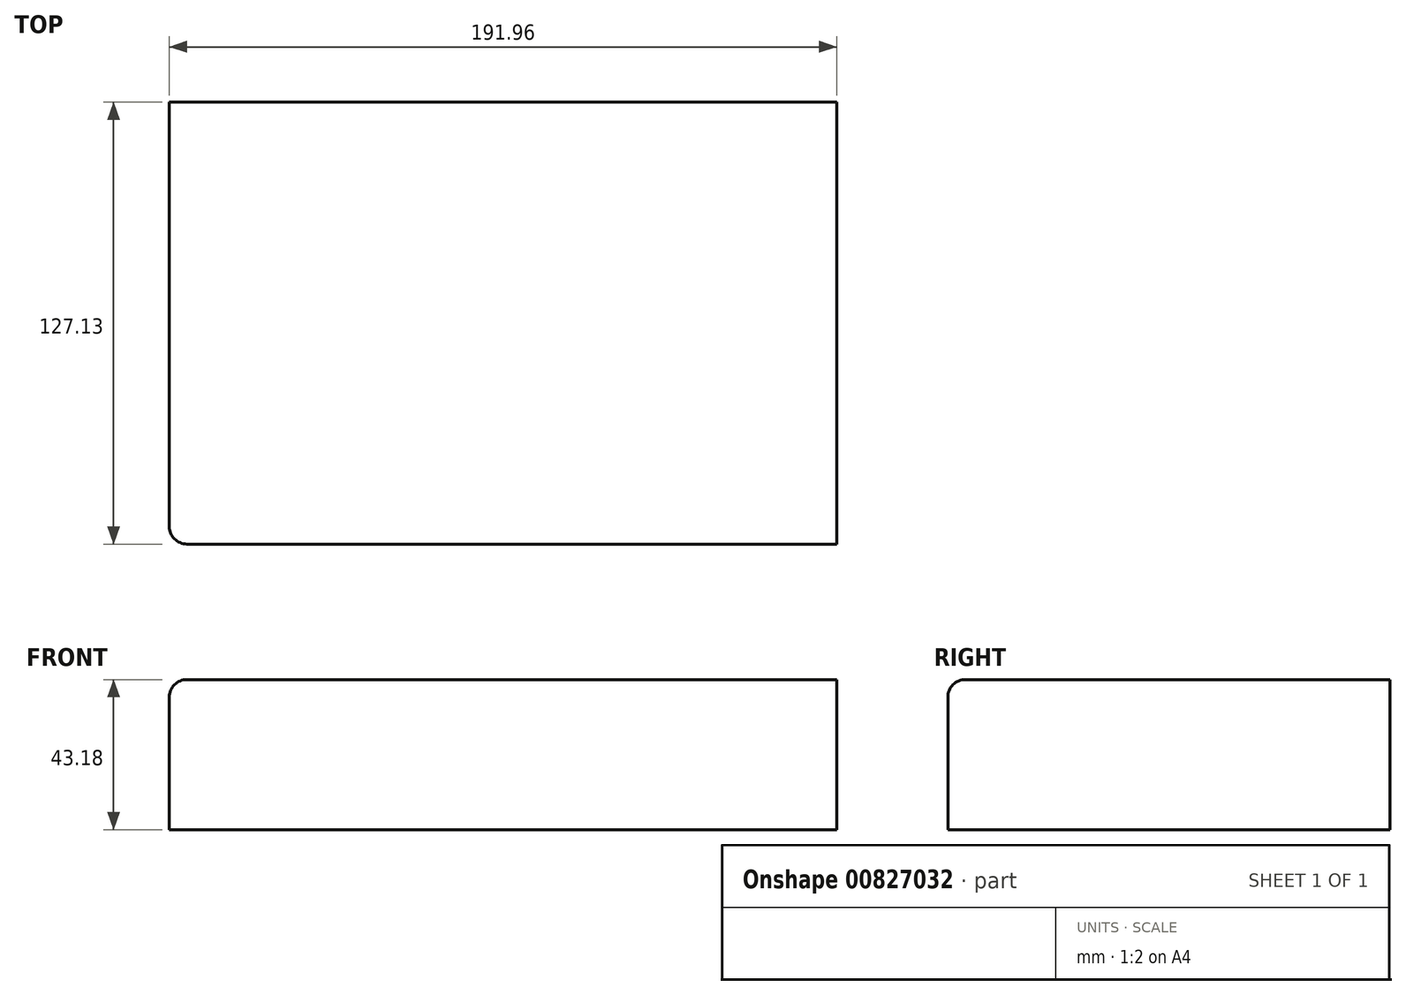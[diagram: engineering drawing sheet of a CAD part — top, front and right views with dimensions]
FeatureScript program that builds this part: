
annotation { "Feature Type Name" : "Feature", "Feature Type Description" : "" }
export const myFeature = defineFeature(function(context is Context, id is Id, definition is map)
    precondition{}
    {
        {
            var Q0;
            Q0=qCreatedBy(makeId("Top.planeOp"),FACE);
            var sketch = newSketch(context, id + "F0", { "sketchPlane" : qUnion([Q0])});
            skLineSegment(sketch, "E0.bottom", {"start": v(-144.56, 74.2) * mm, "end": v(47.4, 74.2) * mm});
            skLineSegment(sketch, "E0.top", {"start": v(-144.56, -52.92) * mm, "end": v(47.4, -52.92) * mm});
            skLineSegment(sketch, "E0.left", {"start": v(-144.56, 74.2) * mm, "end": v(-144.56, -52.92) * mm});
            skLineSegment(sketch, "E0.right", {"start": v(47.4, 74.2) * mm, "end": v(47.4, -52.92) * mm});
            skSolve(sketch);
        }
        {
            var Q0;
            Q0 = qSketchRegion(id + "F0", true);
            extrude(context, id + "F1", {"entities" : qUnion([Q0]), "depth" : 43.18 * mm, "offsetDistance" : 25.4 * mm});
        }
        {
            var Q0;
            Q0=makeQuery(id+"F1.opExtrude","SWEPT_EDGE",EDGE,{"disambiguationData":[OSD([sQuery(id+"F0.wireOp",EDGE,"E0.top"),sQuery(id+"F0.wireOp",EDGE,"E0.left")])]});
            fillet(context, id + "F2", {"entities" : qUnion([Q0]), "radius" : 5.08 * mm, "tangentPropagation" : true, "allowEdgeOverflow" : false});
        }
        {
            var Q0;
            Q0=makeQuery(id+"F1.opExtrude","CAP_EDGE",EDGE,{"disambiguationData":[OSD([sQuery(id+"F0.wireOp",EDGE,"E0.left")])],"isStart":false});
            fillet(context, id + "F3", {"entities" : qUnion([Q0]), "radius" : 5.08 * mm, "tangentPropagation" : true, "allowEdgeOverflow" : false});
        }
    });
